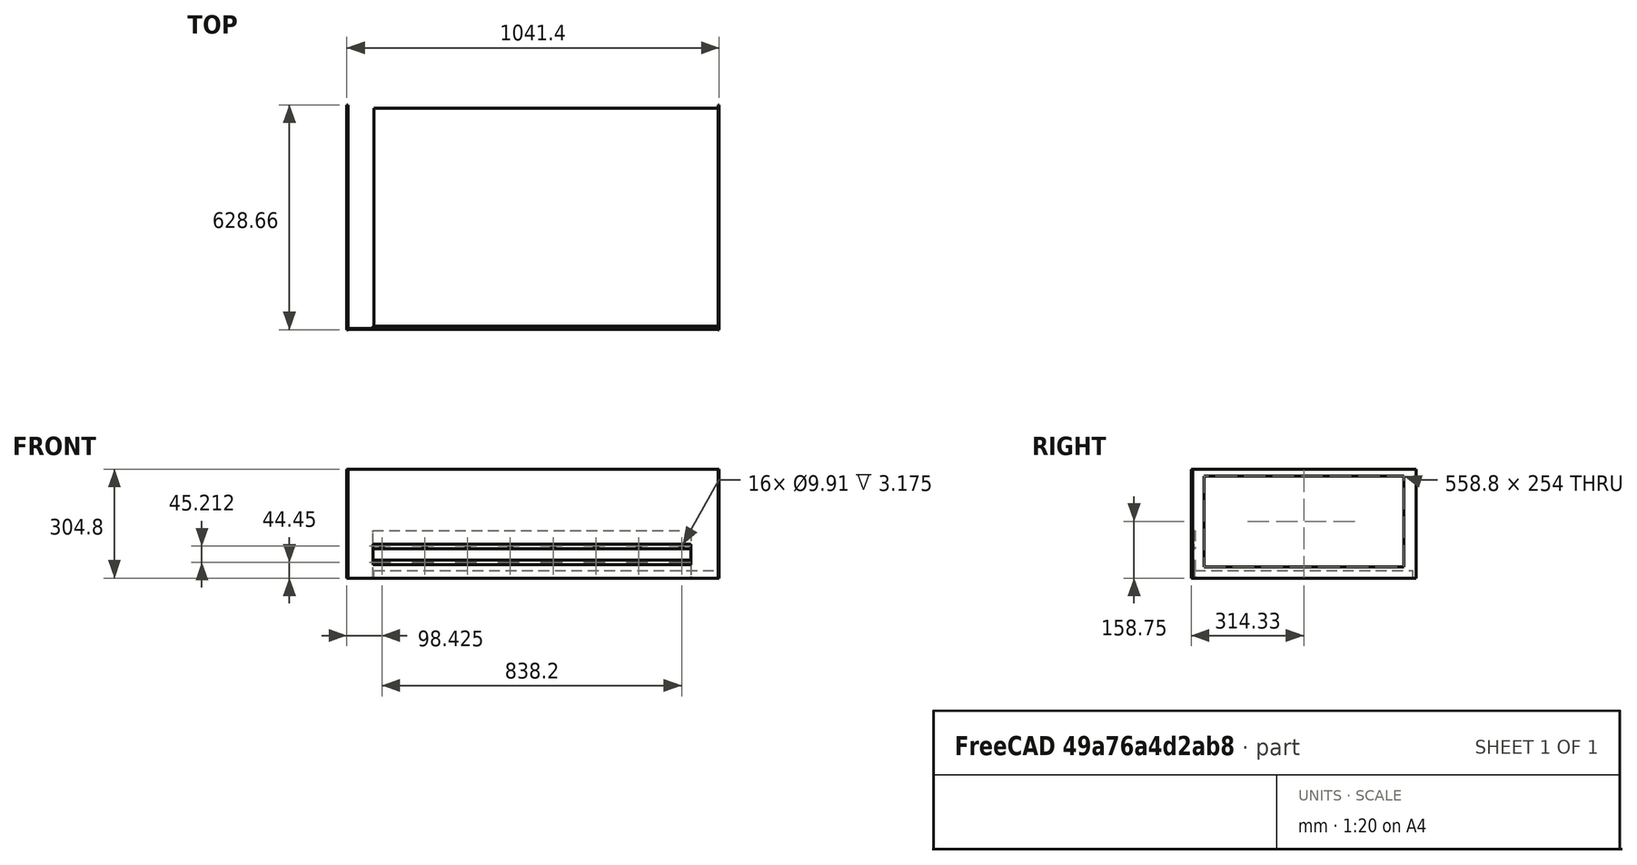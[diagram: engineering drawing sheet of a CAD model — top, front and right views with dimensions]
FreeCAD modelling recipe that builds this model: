
FCSTD DOCUMENT  (FreeCAD 1.1R40971 (Git))
Label: enclosure
License: All rights reserved
LicenseURL: http://en.wikipedia.org/wiki/All_rights_reserved
objects: Sketcher::SketchObject×6, PartDesign::Pad×6, App::Point×6, PartDesign::Body×5, App::Part×1
note: 35 computed .brp shape members not serialized (recipe doc carries the construction recipe); baked Part::Feature solids carry a one-line shape summary decoded from their .brp

FEATURE [Sketcher::SketchObject] Sketch
  ArcFitTolerance = 1e-06
  ExternalTypes = [0]
  FullyConstrained = true
  MakeInternals = false
  sketch-geometry (5):
    g0: LineSegment [constr] StartX=-520.7 StartY=304.8 StartZ=0 EndX=-520.7 EndY=-304.8 EndZ=0
    g1: LineSegment StartX=-444.5 StartY=-304.8 StartZ=0 EndX=520.7 EndY=-304.8 EndZ=0
    g2: LineSegment StartX=520.7 StartY=-304.8 StartZ=0 EndX=520.7 EndY=304.8 EndZ=0
    g3: LineSegment StartX=-444.5 StartY=-304.8 StartZ=0 EndX=-444.5 EndY=304.8 EndZ=0
    g4: LineSegment StartX=-444.5 StartY=304.8 StartZ=0 EndX=520.7 EndY=304.8 EndZ=0
  constraints (16):
    c: Coincident(g3,g4)
    c: Coincident(g1,g3)
    c: PointOnObject(g0,g1)
    c: DistanceX(g1,g1) = 965.2
    c: DistanceY(g2,g2) = 609.6
    c: DistanceX(g0,g1) = 76.2
    c: Vertical(g3)
    c: Vertical(g0)
    c: Coincident(g4,g2)
    c: Horizontal(g4)
    c: Coincident(g2,g1)
    c: PointOnObject(g0,g4)
    c: Symmetric(g1,g0,g-2)
    c: DistanceX(g3,g-1) = 444.5
    c: DistanceX(g0,g-1) = 520.7
    c: Symmetric(g1,g2,g-1)
FEATURE [PartDesign::Pad] Pad
  Direction = (0,0,1)
  Length = 20.32
  Length2 = 10
  Profile = -> Sketch
  ReferenceAxis = -> Sketch [N_Axis]
  Suppressed = false
  Type = 0
FEATURE [PartDesign::Body] Body  label="pad"
  AllowCompound = false
  Group = -> [Sketch,Pad]
  Origin = -> Origin
  Placement = pos=(-0.00178528,0.0656084,0.576416) rot=(0,0,1;0rad)
  Tip = -> Pad
FEATURE [Sketcher::SketchObject] Sketch004  label="outer-sk"
  ArcFitTolerance = 1e-06
  ExternalTypes = [0]
  FullyConstrained = true
  MakeInternals = false
  MapMode = 5
  Placement = pos=(0,-311.15,0) rot=(1,0,0;1.5708rad)
  sketch-geometry (13):
    g0: LineSegment StartX=-520.7 StartY=304.8 StartZ=0 EndX=-520.7 EndY=0 EndZ=0
    g1: LineSegment StartX=-520.7 StartY=0 StartZ=0 EndX=520.7 EndY=0 EndZ=0
    g2: LineSegment StartX=520.7 StartY=0 StartZ=0 EndX=520.7 EndY=304.8 EndZ=0
    g3: LineSegment StartX=520.7 StartY=304.8 StartZ=0 EndX=-520.7 EndY=304.8 EndZ=0
    g4: LineSegment StartX=-447.675 StartY=95.25 StartZ=0 EndX=-447.675 EndY=38.1 EndZ=0
    g5: LineSegment StartX=-447.675 StartY=38.1 StartZ=0 EndX=441.325 EndY=38.1 EndZ=0
    g6: LineSegment StartX=441.325 StartY=38.1 StartZ=0 EndX=441.325 EndY=95.25 EndZ=0
    g7: LineSegment StartX=441.325 StartY=95.25 StartZ=0 EndX=-447.675 EndY=95.25 EndZ=0
    g8: LineSegment [constr] StartX=517.525 StartY=304.8 StartZ=0 EndX=517.525 EndY=0 EndZ=0
    g9: LineSegment [constr] StartX=-517.525 StartY=304.8 StartZ=0 EndX=-517.525 EndY=0 EndZ=0
    g10: LineSegment [constr] StartX=-447.675 StartY=38.1 StartZ=0 EndX=-447.675 EndY=0 EndZ=0
    g11: LineSegment [constr] StartX=-447.675 StartY=50.8 StartZ=0 EndX=441.325 EndY=50.8 EndZ=0
    g12: LineSegment [constr] StartX=441.325 StartY=82.55 StartZ=0 EndX=-447.675 EndY=82.55 EndZ=0
  constraints (43):
    c: Coincident(g0,g1)
    c: Coincident(g1,g2)
    c: Coincident(g2,g3)
    c: Coincident(g3,g0)
    c: Vertical(g0)
    c: Vertical(g2)
    c: Horizontal(g1)
    c: PointOnObject(g1,g-1)
    c: DistanceX(g3,g3) = 1041.4
    c: Coincident(g4,g5)
    c: Coincident(g5,g6)
    c: Coincident(g6,g7)
    c: Coincident(g7,g4)
    c: Vertical(g4)
    c: Vertical(g6)
    c: Horizontal(g5)
    c: Horizontal(g7)
    c: DistanceX(g7,g7) = 889
    c: DistanceY(g-1,g0) = 304.8
    c: DistanceY(g4,g6) = 57.15
    c: Symmetric(g2,g0,g-2)
    c: PointOnObject(g8,g3)
    c: PointOnObject(g8,g1)
    c: Vertical(g8)
    c: DistanceX(g8,g1) = 3.175
    c: PointOnObject(g9,g1)
    c: Vertical(g9)
    c: Symmetric(g9,g8,g-2)
    c: PointOnObject(g10,g5)
    c: PointOnObject(g10,g1)
    c: Vertical(g10)
    c: DistanceX(g10,g8) = 965.2
    c: DistanceX(g9,g10) = 69.85
    c: DistanceX(g9,g4) = 69.85
    c: PointOnObject(g11,g4)
    c: PointOnObject(g11,g6)
    c: Horizontal(g11)
    c: PointOnObject(g12,g6)
    c: PointOnObject(g12,g4)
    c: Horizontal(g12)
    c: DistanceY(g11,g12) = 31.75
    c: DistanceY(g10,g11) = 50.8
    c: DistanceY(g10,g11) = 12.7
FEATURE [PartDesign::Pad] Pad002  label="outer"
  Direction = (0,-1,-2e-16)
  Length = 2.54
  Length2 = 10
  Placement = pos=(0,-311.15,0) rot=(1,0,0;1.5708rad)
  Profile = -> Sketch004
  ReferenceAxis = -> Sketch004 [N_Axis]
  Suppressed = false
  Type = 0
FEATURE [Sketcher::SketchObject] Sketch005  label="magnet-holder"
  ArcFitTolerance = 1e-06
  ExternalTypes = [0]
  FullyConstrained = true
  MakeInternals = false
  MapMode = 5
  Placement = pos=(0,-311.15,0) rot=(1,0,0;1.5708rad)
  sketch-geometry (43):
    g0: LineSegment StartX=-447.675 StartY=0 StartZ=0 EndX=-447.675 EndY=50.8 EndZ=0
    g1: LineSegment StartX=-447.675 StartY=82.55 StartZ=0 EndX=441.325 EndY=82.55 EndZ=0
    g2: LineSegment StartX=441.325 StartY=50.8 StartZ=0 EndX=441.325 EndY=0 EndZ=0
    g3: LineSegment StartX=441.325 StartY=0 StartZ=0 EndX=-447.675 EndY=0 EndZ=0
    g4: LineSegment StartX=-447.675 StartY=82.55 StartZ=0 EndX=-447.675 EndY=133.35 EndZ=0
    g5: LineSegment StartX=-447.675 StartY=133.35 StartZ=0 EndX=441.325 EndY=133.35 EndZ=0
    g6: LineSegment StartX=441.325 StartY=133.35 StartZ=0 EndX=441.325 EndY=82.55 EndZ=0
    g7: LineSegment StartX=441.325 StartY=50.8 StartZ=0 EndX=-447.675 EndY=50.8 EndZ=0
    g8: LineSegment [constr] StartX=-447.675 StartY=89.662 StartZ=0 EndX=441.325 EndY=89.662 EndZ=0
    g9: LineSegment [constr] StartX=441.325 StartY=44.45 StartZ=0 EndX=-447.675 EndY=44.45 EndZ=0
    g10: Circle CenterX=-422.275 CenterY=89.662 CenterZ=0 NormalX=0 NormalY=0 NormalZ=1 AngleXU=0 Radius=4.953
    g11: Circle CenterX=-302.532 CenterY=89.662 CenterZ=0 NormalX=0 NormalY=0 NormalZ=1 AngleXU=0 Radius=4.953
    g12: Circle CenterX=-182.789 CenterY=89.662 CenterZ=0 NormalX=0 NormalY=0 NormalZ=1 AngleXU=0 Radius=4.953
    g13: Circle CenterX=-63.0464 CenterY=89.662 CenterZ=0 NormalX=0 NormalY=0 NormalZ=1 AngleXU=0 Radius=4.953
    g14: Circle CenterX=56.6964 CenterY=89.662 CenterZ=0 NormalX=0 NormalY=0 NormalZ=1 AngleXU=0 Radius=4.953
    g15: Circle CenterX=176.439 CenterY=89.662 CenterZ=0 NormalX=0 NormalY=0 NormalZ=1 AngleXU=0 Radius=4.953
    g16: Circle CenterX=296.182 CenterY=89.662 CenterZ=0 NormalX=0 NormalY=0 NormalZ=1 AngleXU=0 Radius=4.953
    g17: Circle CenterX=415.925 CenterY=89.662 CenterZ=0 NormalX=0 NormalY=0 NormalZ=1 AngleXU=0 Radius=4.953
    g18: LineSegment [constr] StartX=-422.275 StartY=89.662 StartZ=0 EndX=-302.532 EndY=89.662 EndZ=0
    g19: LineSegment [constr] StartX=-302.532 StartY=89.662 StartZ=0 EndX=-182.789 EndY=89.662 EndZ=0
    g20: LineSegment [constr] StartX=-182.789 StartY=89.662 StartZ=0 EndX=-63.0464 EndY=89.662 EndZ=0
    g21: LineSegment [constr] StartX=-63.0464 StartY=89.662 StartZ=0 EndX=56.6964 EndY=89.662 EndZ=0
    g22: LineSegment [constr] StartX=56.6964 StartY=89.662 StartZ=0 EndX=176.439 EndY=89.662 EndZ=0
    g23: LineSegment [constr] StartX=176.439 StartY=89.662 StartZ=0 EndX=296.182 EndY=89.662 EndZ=0
    g24: LineSegment [constr] StartX=296.182 StartY=89.662 StartZ=0 EndX=415.925 EndY=89.662 EndZ=0
    g25: GeomPoint [constr] X=-3.175 Y=89.662 Z=0
    g26: Circle CenterX=-422.275 CenterY=44.45 CenterZ=0 NormalX=0 NormalY=0 NormalZ=1 AngleXU=0 Radius=4.953
    g27: Circle CenterX=-302.532 CenterY=44.45 CenterZ=0 NormalX=0 NormalY=0 NormalZ=1 AngleXU=0 Radius=4.953
    g28: Circle CenterX=-182.789 CenterY=44.45 CenterZ=0 NormalX=0 NormalY=0 NormalZ=1 AngleXU=0 Radius=4.953
    g29: Circle CenterX=-63.0464 CenterY=44.45 CenterZ=0 NormalX=0 NormalY=0 NormalZ=1 AngleXU=0 Radius=4.953
    g30: Circle CenterX=56.6964 CenterY=44.45 CenterZ=0 NormalX=0 NormalY=0 NormalZ=1 AngleXU=0 Radius=4.953
    g31: Circle CenterX=176.439 CenterY=44.45 CenterZ=0 NormalX=0 NormalY=0 NormalZ=1 AngleXU=0 Radius=4.953
    g32: Circle CenterX=296.182 CenterY=44.45 CenterZ=0 NormalX=0 NormalY=0 NormalZ=1 AngleXU=0 Radius=4.953
    g33: Circle CenterX=415.925 CenterY=44.45 CenterZ=0 NormalX=0 NormalY=0 NormalZ=1 AngleXU=0 Radius=4.953
    g34: LineSegment [constr] StartX=-422.275 StartY=44.45 StartZ=0 EndX=-302.532 EndY=44.45 EndZ=0
    g35: LineSegment [constr] StartX=-302.532 StartY=44.45 StartZ=0 EndX=-182.789 EndY=44.45 EndZ=0
    g36: LineSegment [constr] StartX=-182.789 StartY=44.45 StartZ=0 EndX=-63.0464 EndY=44.45 EndZ=0
    g37: LineSegment [constr] StartX=-63.0464 StartY=44.45 StartZ=0 EndX=56.6964 EndY=44.45 EndZ=0
    g38: LineSegment [constr] StartX=56.6964 StartY=44.45 StartZ=0 EndX=176.439 EndY=44.45 EndZ=0
    g39: LineSegment [constr] StartX=176.439 StartY=44.45 StartZ=0 EndX=296.182 EndY=44.45 EndZ=0
    g40: LineSegment [constr] StartX=296.182 StartY=44.45 StartZ=0 EndX=415.925 EndY=44.45 EndZ=0
    g41: LineSegment [constr] StartX=-517.525 StartY=304.8 StartZ=0 EndX=-517.525 EndY=0 EndZ=0
    g42: LineSegment [constr] StartX=517.525 StartY=304.8 StartZ=0 EndX=517.525 EndY=0 EndZ=0
  constraints (117):
    c: Coincident(g2,g3)
    c: Coincident(g3,g0)
    c: Vertical(g0)
    c: Vertical(g2)
    c: Horizontal(g1)
    c: Horizontal(g3)
    c: PointOnObject(g0,g-1)
    c: Coincident(g4,g5)
    c: Coincident(g5,g6)
    c: Vertical(g4)
    c: Vertical(g6)
    c: Horizontal(g5)
    c: Horizontal(g7)
    c: PointOnObject(g7,g2)
    c: DistanceY(g7,g1) = 31.75
    c: DistanceX(g3,g3) = 889
    c: PointOnObject(g9,g4)
    c: Horizontal(g9)
    c: Horizontal(g8)
    c: PointOnObject(g8,g0)
    c: PointOnObject(g8,g2)
    c: PointOnObject(g9,g2)
    c: DistanceY(g1,g8) = 7.112
    c: DistanceY(g9,g7) = 6.35
    c: Diameter(g10) = 9.906
    c: Coincident(g18,g10)
    c: Coincident(g18,g11)
    c: Horizontal(g18)
    c: Coincident(g19,g11)
    c: Coincident(g19,g12)
    c: Horizontal(g19)
    c: Coincident(g20,g12)
    c: Coincident(g20,g13)
    c: Horizontal(g20)
    c: Coincident(g21,g13)
    c: Coincident(g21,g14)
    c: Horizontal(g21)
    c: Coincident(g22,g14)
    c: Horizontal(g22)
    c: Coincident(g23,g15)
    c: Coincident(g23,g16)
    c: Horizontal(g23)
    c: Coincident(g24,g16)
    c: Coincident(g24,g17)
    c: Horizontal(g24)
    c: Equal(g24,g23)
    c: Equal(g23,g22)
    c: Equal(g22,g21)
    c: Equal(g21,g20)
    c: Equal(g20,g19)
    c: Equal(g19,g18)
    c: DistanceX(g10,g17) = 838.2
    c: Coincident(g22,g15)
    c: Equal(g17,g16)
    c: Equal(g16,g15)
    c: Equal(g15,g14)
    c: Equal(g14,g13)
    c: Equal(g13,g12)
    c: Equal(g12,g11)
    c: Equal(g11,g10)
    c: Symmetric(g21,g21,g25)
    c: Symmetric(g8,g8,g25)
    c: Equal(g26,g10)
    c: Coincident(g34,g26)
    c: Coincident(g34,g27)
    c: Horizontal(g34)
    c: Coincident(g35,g27)
    c: Coincident(g35,g28)
    c: Horizontal(g35)
    c: Coincident(g36,g28)
    c: Coincident(g36,g29)
    c: Horizontal(g36)
    c: Coincident(g37,g29)
    c: Coincident(g37,g30)
    c: Horizontal(g37)
    c: Coincident(g38,g30)
    c: Coincident(g38,g31)
    c: Horizontal(g38)
    c: Coincident(g39,g31)
    c: Coincident(g39,g32)
    c: Horizontal(g39)
    c: Coincident(g40,g32)
    c: Coincident(g40,g33)
    c: Horizontal(g40)
    c: Equal(g34,g35)
    c: Equal(g35,g36)
    c: Equal(g36,g37)
    c: Equal(g37,g38)
    c: Equal(g38,g39)
    c: Equal(g39,g40)
    c: Vertical(g26,g10)
    c: PointOnObject(g26,g9)
    c: Vertical(g33,g17)
    c: Equal(g27,g29)
    c: Equal(g29,g30)
    c: Equal(g30,g31)
    c: Equal(g31,g32)
    c: Equal(g32,g33)
    c: Equal(g28,g27)
    c: Equal(g11,g27)
    c: Vertical(g41)
    c: PointOnObject(g42,g-1)
    c: Vertical(g42)
    c: DistanceY(g41,g41) = 304.8
    c: PointOnObject(g41,g-1)
    c: Symmetric(g42,g41,g-2)
    c: DistanceX(g41,g42) = 1035.05
    c: DistanceX(g41,g9) = 69.85
    c: PointOnObject(g2,g7)
    c: Coincident(g0,g7)
    c: PointOnObject(g4,g1)
    c: Equal(g0,g4)
    c: DistanceX(g5,g5) = 889
    c: Vertical(g0,g1)
    c: PointOnObject(g9,g0)
    c: Coincident(g1,g6)
    c: DistanceY(g0,g0) = 50.8
FEATURE [Sketcher::SketchObject] Sketch006  label="magnet-backersk"
  ArcFitTolerance = 1e-06
  ExternalTypes = [0]
  FullyConstrained = true
  MakeInternals = false
  MapMode = 5
  Placement = pos=(0,-307.975,0) rot=(1,0,0;1.5708rad)
  expr: Constraints[8] = 12 in
  sketch-geometry (10):
    g0: LineSegment StartX=-447.675 StartY=50.8 StartZ=0 EndX=441.325 EndY=50.8 EndZ=0
    g1: LineSegment StartX=441.325 StartY=0 StartZ=0 EndX=-447.675 EndY=0 EndZ=0
    g2: LineSegment [constr] StartX=-517.525 StartY=304.8 StartZ=0 EndX=-517.525 EndY=0 EndZ=0
    g3: LineSegment [constr] StartX=517.525 StartY=304.8 StartZ=0 EndX=517.525 EndY=0 EndZ=0
    g4: LineSegment StartX=-447.675 StartY=50.8 StartZ=0 EndX=-447.675 EndY=0 EndZ=0
    g5: LineSegment StartX=441.325 StartY=50.8 StartZ=0 EndX=441.325 EndY=0 EndZ=0
    g6: LineSegment StartX=-447.675 StartY=133.35 StartZ=0 EndX=-447.675 EndY=82.55 EndZ=0
    g7: LineSegment StartX=-447.675 StartY=82.55 StartZ=0 EndX=441.325 EndY=82.55 EndZ=0
    g8: LineSegment StartX=441.325 StartY=82.55 StartZ=0 EndX=441.325 EndY=133.35 EndZ=0
    g9: LineSegment StartX=441.325 StartY=133.35 StartZ=0 EndX=-447.675 EndY=133.35 EndZ=0
  constraints (32):
    c: Horizontal(g0)
    c: Horizontal(g1)
    c: DistanceY(g1,g0) = 50.8
    c: Vertical(g2)
    c: PointOnObject(g2,g-1)
    c: PointOnObject(g3,g-1)
    c: Vertical(g3)
    c: Symmetric(g3,g2,g-2)
    c: DistanceY(g2,g2) = 304.8
    c: DistanceY(g2,g2) = 304.8
    c: DistanceX(g2,g3) = 1035.05
    c: Coincident(g4,g0)
    c: Coincident(g4,g1)
    c: Vertical(g4)
    c: Coincident(g5,g0)
    c: Coincident(g5,g1)
    c: Vertical(g5)
    c: DistanceX(g0,g0) = 889
    c: DistanceX(g2,g1) = 69.85
    c: PointOnObject(g1,g-1)
    c: Coincident(g6,g7)
    c: Coincident(g7,g8)
    c: Coincident(g8,g9)
    c: Coincident(g9,g6)
    c: Vertical(g6)
    c: Vertical(g8)
    c: Horizontal(g7)
    c: Horizontal(g9)
    c: PointOnObject(g7,g5)
    c: PointOnObject(g6,g4)
    c: DistanceY(g0,g6) = 31.75
    c: Equal(g6,g4)
FEATURE [Sketcher::SketchObject] Sketch007
  ArcFitTolerance = 1e-06
  ExternalTypes = [0]
  FullyConstrained = true
  MakeInternals = false
  MapMode = 5
  Placement = pos=(-520.7,0,0) rot=(0.57735,0.57735,0.57735;2.0944rad)
  sketch-geometry (4):
    g0: LineSegment StartX=-314.325 StartY=304.8 StartZ=0 EndX=-314.325 EndY=0 EndZ=0
    g1: LineSegment StartX=-314.325 StartY=0 StartZ=0 EndX=314.325 EndY=0 EndZ=0
    g2: LineSegment StartX=314.325 StartY=0 StartZ=0 EndX=314.325 EndY=304.8 EndZ=0
    g3: LineSegment StartX=314.325 StartY=304.8 StartZ=0 EndX=-314.325 EndY=304.8 EndZ=0
  constraints (11):
    c: Coincident(g0,g1)
    c: Coincident(g1,g2)
    c: Coincident(g2,g3)
    c: Coincident(g3,g0)
    c: Vertical(g0)
    c: Vertical(g2)
    c: Horizontal(g1)
    c: PointOnObject(g1,g-1)
    c: DistanceY(g2,g2) = 304.8
    c: DistanceX(g3,g3) = 628.65
    c: Symmetric(g0,g2,g-2)
FEATURE [PartDesign::Body] Body004  label="back"
  AllowCompound = false
  Origin = -> Origin010
FEATURE [Sketcher::SketchObject] Sketch008
  ArcFitTolerance = 1e-06
  ExternalTypes = [0]
  FullyConstrained = true
  MakeInternals = false
  MapMode = 5
  Placement = pos=(520.7,0,0) rot=(0.57735,0.57735,0.57735;2.0944rad)
  sketch-geometry (8):
    g0: LineSegment StartX=-314.325 StartY=304.8 StartZ=0 EndX=-314.325 EndY=0 EndZ=0
    g1: LineSegment StartX=-314.325 StartY=0 StartZ=0 EndX=314.325 EndY=0 EndZ=0
    g2: LineSegment StartX=314.325 StartY=0 StartZ=0 EndX=314.325 EndY=304.8 EndZ=0
    g3: LineSegment StartX=314.325 StartY=304.8 StartZ=0 EndX=-314.325 EndY=304.8 EndZ=0
    g4: LineSegment StartX=-279.4 StartY=285.75 StartZ=0 EndX=-279.4 EndY=31.75 EndZ=0
    g5: LineSegment StartX=-279.4 StartY=31.75 StartZ=0 EndX=279.4 EndY=31.75 EndZ=0
    g6: LineSegment StartX=279.4 StartY=31.75 StartZ=0 EndX=279.4 EndY=285.75 EndZ=0
    g7: LineSegment StartX=279.4 StartY=285.75 StartZ=0 EndX=-279.4 EndY=285.75 EndZ=0
  constraints (22):
    c: Coincident(g0,g1)
    c: Coincident(g1,g2)
    c: Coincident(g2,g3)
    c: Coincident(g3,g0)
    c: Vertical(g0)
    c: Vertical(g2)
    c: Horizontal(g1)
    c: PointOnObject(g1,g-1)
    c: DistanceX(g3,g3) = 628.65
    c: Symmetric(g0,g2,g-2)
    c: DistanceY(g0,g0) = 304.8
    c: Coincident(g4,g5)
    c: Coincident(g5,g6)
    c: Coincident(g6,g7)
    c: Coincident(g7,g4)
    c: Vertical(g4)
    c: Vertical(g6)
    c: Horizontal(g7)
    c: Symmetric(g5,g4,g-2)
    c: DistanceX(g5,g5) = 558.8
    c: DistanceY(g6,g6) = 254
    c: DistanceY(g-1,g5) = 31.75
FEATURE [PartDesign::Pad] Pad006
  Direction = (1,0,0)
  Length = 2.54
  Length2 = 10
  Placement = pos=(520.7,0,0) rot=(0.57735,0.57735,0.57735;2.0944rad)
  Profile = -> Sketch008
  ReferenceAxis = -> Sketch008 [N_Axis]
  Reversed = true
  Suppressed = false
  Type = 0
FEATURE [PartDesign::Body] Body006  label="right"
  AllowCompound = false
  Group = -> [Sketch008,Pad006]
  Origin = -> Origin014
  Tip = -> Pad006
FEATURE [PartDesign::Pad] Pad007
  Direction = (1,0,0)
  Length = 3.175
  Length2 = 10
  Placement = pos=(-520.7,0,0) rot=(0.57735,0.57735,0.57735;2.0944rad)
  Profile = -> Sketch007
  ReferenceAxis = -> Sketch007 [N_Axis]
  Suppressed = false
  Type = 0
FEATURE [PartDesign::Body] Body005  label="left"
  AllowCompound = false
  Group = -> [Sketch007,Pad007]
  Origin = -> Origin012
  Tip = -> Pad007
FEATURE [PartDesign::Pad] Pad008
  BaseFeature = -> Pad002
  Direction = (0,-1,-2e-16)
  Length = 3.175
  Length2 = 10
  Placement = pos=(0,-311.15,0) rot=(1,0,0;1.5708rad)
  Profile = -> Sketch005
  ReferenceAxis = -> Sketch005 [N_Axis]
  Reversed = true
  Suppressed = false
  Type = 0
FEATURE [PartDesign::Pad] Pad009
  BaseFeature = -> Pad008
  Direction = (0,-1,-2e-16)
  Length = 3.175
  Length2 = 10
  Placement = pos=(0,-311.15,0) rot=(1,0,0;1.5708rad)
  Profile = -> Sketch006
  ReferenceAxis = -> Sketch006 [N_Axis]
  Reversed = true
  Suppressed = false
  Type = 0
FEATURE [PartDesign::Body] Body003  label="front"
  AllowCompound = false
  Group = -> [Sketch004,Pad002,Sketch005,Sketch006,Pad008,Pad009]
  Origin = -> Origin008
  Tip = -> Pad009
FEATURE [App::Part] Part  label="enclosure"
  Group = -> [Body,Body003,Body004,Body005,Body006]
  Origin = -> Origin004
FEATURE [App::Point] Origin015  label="Origin"
  Role = Origin
FEATURE [App::Point] Origin017  label="Origin"
  Role = Origin
FEATURE [App::Point] Origin018  label="Origin"
  Role = Origin
FEATURE [App::Point] Origin019  label="Origin"
  Role = Origin
FEATURE [App::Point] Origin020  label="Origin"
  Role = Origin
FEATURE [App::Point] Origin021  label="Origin"
  Role = Origin
